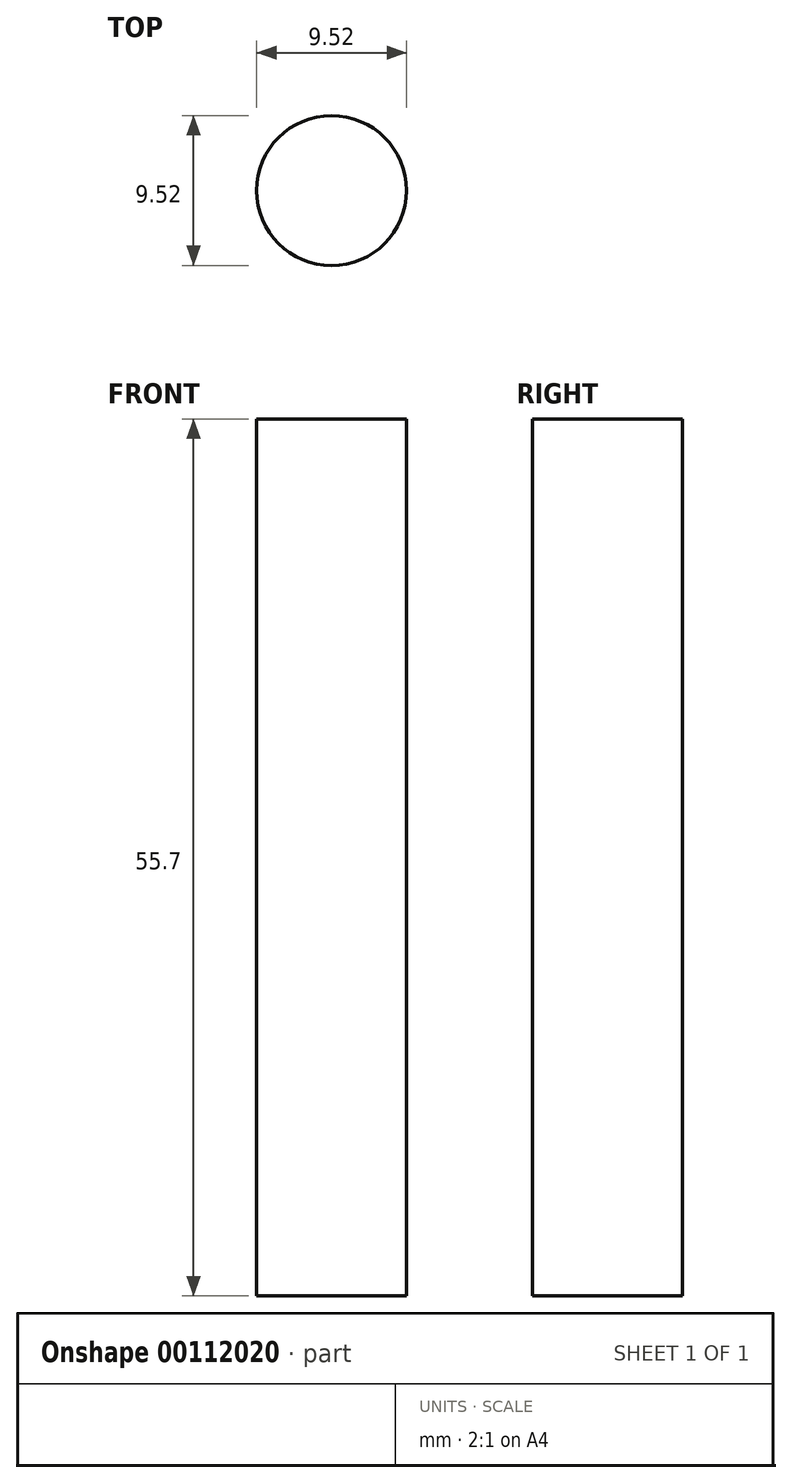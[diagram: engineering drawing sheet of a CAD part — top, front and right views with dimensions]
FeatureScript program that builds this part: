
annotation { "Feature Type Name" : "Feature", "Feature Type Description" : "" }
export const myFeature = defineFeature(function(context is Context, id is Id, definition is map)
    precondition{}
    {
        {
            var Q0;
            Q0=qCreatedBy(makeId("Top.planeOp"),FACE);
            var sketch = newSketch(context, id + "F0", { "sketchPlane" : qUnion([Q0])});
            skCircle(sketch, "E0", {"center": v(0, 0) * mm, "radius": 4.76 * mm});
            skSolve(sketch);
        }
        {
            var Q0;
            Q0=qSketchRegion(id+"F0",true);
            extrude(context, id + "F1", {"entities" : qUnion([Q0]), "depth" : (20 + 12.7 + 23) * mm});
        }
    });
